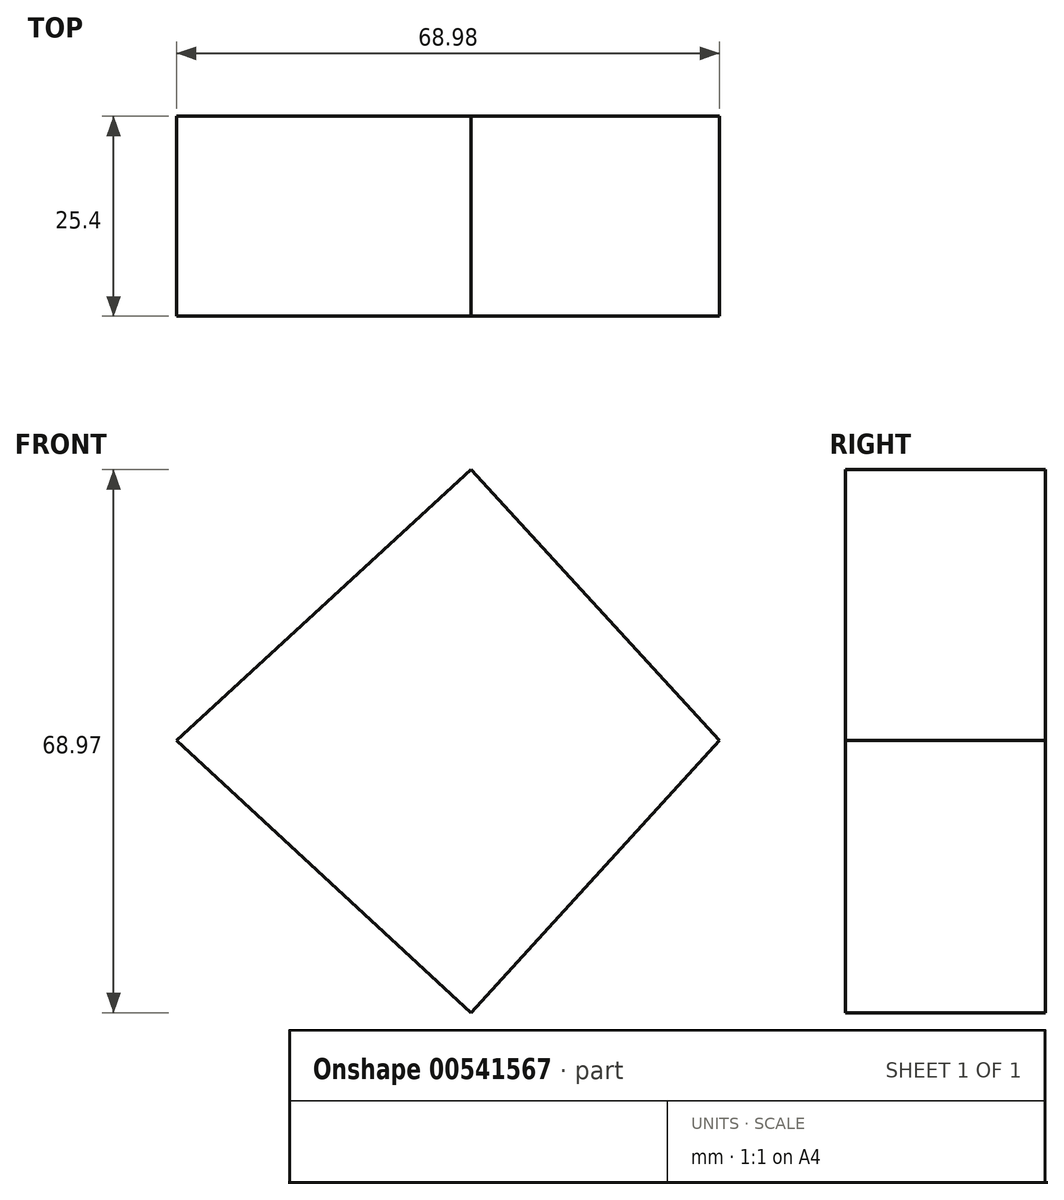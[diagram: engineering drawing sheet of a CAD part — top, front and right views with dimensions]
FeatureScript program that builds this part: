
annotation { "Feature Type Name" : "Feature", "Feature Type Description" : "" }
export const myFeature = defineFeature(function(context is Context, id is Id, definition is map)
    precondition{}
    {
        {
            var Q0;
            Q0=qCreatedBy(makeId("Front.planeOp"),FACE);
            var sketch = newSketch(context, id + "F0", { "sketchPlane" : qUnion([Q0])});
            skLineSegment(sketch, "E0", {"start": v(-37.42, 0) * mm, "end": v(0, 34.36) * mm});
            skLineSegment(sketch, "E1", {"start": v(0, 34.36) * mm, "end": v(31.56, 0) * mm});
            skLineSegment(sketch, "E2", {"start": v(31.56, 0) * mm, "end": v(0, -34.61) * mm});
            skLineSegment(sketch, "E3", {"start": v(0, -34.61) * mm, "end": v(-37.42, 0) * mm});
            skLineSegment(sketch, "E4", {"start": v(-18.7, 17.18) * mm, "end": v(15.78, 17.18) * mm, "construction": true});
            skLineSegment(sketch, "E5", {"start": v(15.78, 17.18) * mm, "end": v(15.78, -17.3) * mm, "construction": true});
            skLineSegment(sketch, "E6", {"start": v(15.78, -17.3) * mm, "end": v(-18.7, -17.3) * mm, "construction": true});
            skLineSegment(sketch, "E7", {"start": v(-18.7, -17.3) * mm, "end": v(-18.7, 17.18) * mm, "construction": true});
            skSolve(sketch);
        }
        {
            var Q0;
            Q0 = qSketchRegion(id + "F0", true);
            extrude(context, id + "F1", {"entities" : qUnion([Q0]), "depth" : 25.4 * mm, "offsetDistance" : 25.4 * mm});
        }
    });
